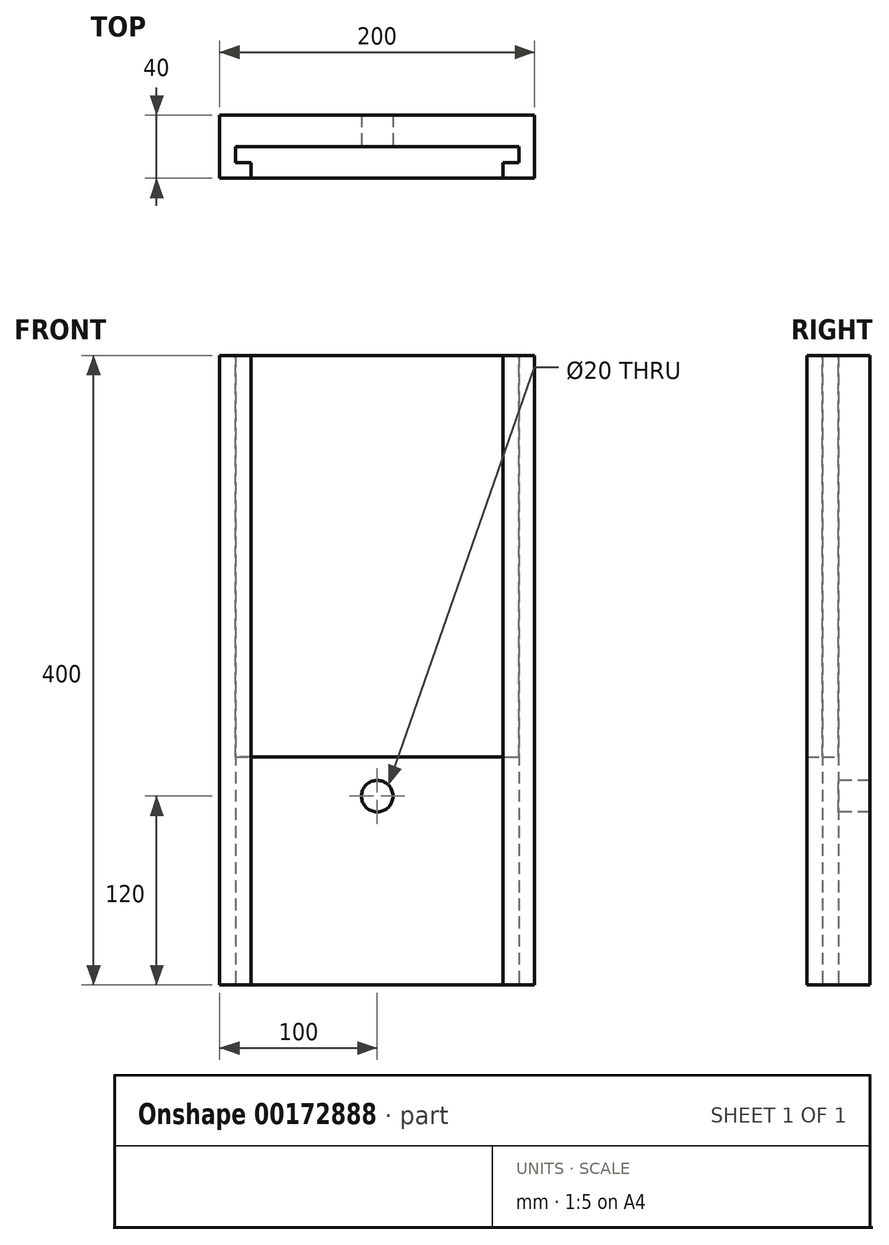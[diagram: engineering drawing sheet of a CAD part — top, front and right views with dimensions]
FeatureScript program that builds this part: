
annotation { "Feature Type Name" : "Feature", "Feature Type Description" : "" }
export const myFeature = defineFeature(function(context is Context, id is Id, definition is map)
    precondition{}
    {
        {
            var Q0;
            Q0=qCreatedBy(makeId("Top.planeOp"),FACE);
            var sketch = newSketch(context, id + "F0", { "sketchPlane" : qUnion([Q0])});
            skLineSegment(sketch, "E0", {"start": v(0, 40) * mm, "end": v(100, 40) * mm});
            skLineSegment(sketch, "E1", {"start": v(100, 40) * mm, "end": v(100, 0) * mm});
            skLineSegment(sketch, "E2", {"start": v(100, 0) * mm, "end": v(80, 0) * mm});
            skLineSegment(sketch, "E3", {"start": v(80, 0) * mm, "end": v(80, 10) * mm});
            skLineSegment(sketch, "E4", {"start": v(80, 10) * mm, "end": v(90, 10) * mm});
            skLineSegment(sketch, "E5", {"start": v(90, 10) * mm, "end": v(90, 20) * mm});
            skLineSegment(sketch, "E6", {"start": v(90, 20) * mm, "end": v(0, 20) * mm});
            skLineSegment(sketch, "E7", {"start": v(0, 40) * mm, "end": v(0, 0) * mm, "construction": true});
            skLineSegment(sketch, "E8.MirrorCS", {"start": v(0, 40) * mm, "end": v(-100, 40) * mm});
            skLineSegment(sketch, "E9.MirrorCS", {"start": v(-100, 40) * mm, "end": v(-100, 0) * mm});
            skLineSegment(sketch, "E10.MirrorCS", {"start": v(-100, 0) * mm, "end": v(-80, 0) * mm});
            skLineSegment(sketch, "E11.MirrorCS", {"start": v(-80, 0) * mm, "end": v(-80, 10) * mm});
            skLineSegment(sketch, "E12.MirrorCS", {"start": v(-80, 10) * mm, "end": v(-90, 10) * mm});
            skLineSegment(sketch, "E13.MirrorCS", {"start": v(-90, 10) * mm, "end": v(-90, 20) * mm});
            skLineSegment(sketch, "E14.MirrorCS", {"start": v(-90, 20) * mm, "end": v(0, 20) * mm});
            skSolve(sketch);
        }
        {
            var Q0;
            Q0 = qSketchRegion(id + "F0", true);
            extrude(context, id + "F1", {"entities" : qUnion([Q0]), "depth" : 280 * mm, "hasSecondDirection" : true, "secondDirectionOppositeDirection" : true, "secondDirectionDepth" : 120 * mm});
        }
        {
            var Q0;
            Q0=makeQuery(id+"F1.opExtrude","SWEPT_FACE",FACE,{"disambiguationData":[OSD([sQuery(id+"F0.wireOp",EDGE,"E6"),sQuery(id+"F0.wireOp",EDGE,"E14.MirrorCS")])]});
            var sketch = newSketch(context, id + "F2", { "sketchPlane" : qUnion([Q0])});
            skCircle(sketch, "E15", {"center": v(0, 0) * mm, "radius": 10 * mm});
            skSolve(sketch);
        }
        {
            var Q0;
            Q0 = qSketchRegion(id + "F2", true);
            extrude(context, id + "F3", {"entities" : qUnion([Q0]), "operationType" : NewBodyOperationType.REMOVE, "oppositeDirection" : true, "depth" : 20 * mm});
        }
        {
            var Q0;
            Q0=makeQuery(id+"F1.opExtrude","CAP_FACE",FACE,{"disambiguationData":[OSD([sQuery(id+"F0.wireOp",EDGE,"E0"),sQuery(id+"F0.wireOp",EDGE,"E1"),sQuery(id+"F0.wireOp",EDGE,"E2"),sQuery(id+"F0.wireOp",EDGE,"E3"),sQuery(id+"F0.wireOp",EDGE,"E4"),sQuery(id+"F0.wireOp",EDGE,"E5"),sQuery(id+"F0.wireOp",EDGE,"E6"),sQuery(id+"F0.wireOp",EDGE,"E8.MirrorCS"),sQuery(id+"F0.wireOp",EDGE,"E9.MirrorCS"),sQuery(id+"F0.wireOp",EDGE,"E10.MirrorCS"),sQuery(id+"F0.wireOp",EDGE,"E11.MirrorCS"),sQuery(id+"F0.wireOp",EDGE,"E12.MirrorCS"),sQuery(id+"F0.wireOp",EDGE,"E13.MirrorCS"),sQuery(id+"F0.wireOp",EDGE,"E14.MirrorCS")])],"isStart":false});
            var sketch = newSketch(context, id + "F4", { "sketchPlane" : qUnion([Q0])});
            skLineSegment(sketch, "E16", {"start": v(90, 20) * mm, "end": v(-90, 20) * mm});
            skLineSegment(sketch, "E17", {"start": v(-90, 20) * mm, "end": v(-90, 10) * mm});
            skLineSegment(sketch, "E18", {"start": v(-90, 10) * mm, "end": v(-80, 10) * mm});
            skLineSegment(sketch, "E19", {"start": v(-80, 10) * mm, "end": v(-80, 0) * mm});
            skLineSegment(sketch, "E20", {"start": v(-80, 0) * mm, "end": v(80, 0) * mm});
            skLineSegment(sketch, "E21", {"start": v(80, 0) * mm, "end": v(80, 10) * mm});
            skLineSegment(sketch, "E22", {"start": v(80, 10) * mm, "end": v(90, 10) * mm});
            skLineSegment(sketch, "E23", {"start": v(90, 10) * mm, "end": v(90, 20) * mm});
            skSolve(sketch);
        }
        {
            var Q0;
            Q0=makeQuery(id+"F4.imprint","IMPRINT",FACE,{"disambiguationData":[TD([[makeQuery(id+"F4.imprint","IMPRINT",EDGE,{"derivedFrom":sQuery(id+"F4.wireOp",EDGE,"E16")}),-1.0]])]});
            extrude(context, id + "F5", {"entities" : qUnion([Q0]), "oppositeDirection" : true, "depth" : 255 * mm});
        }
    });
